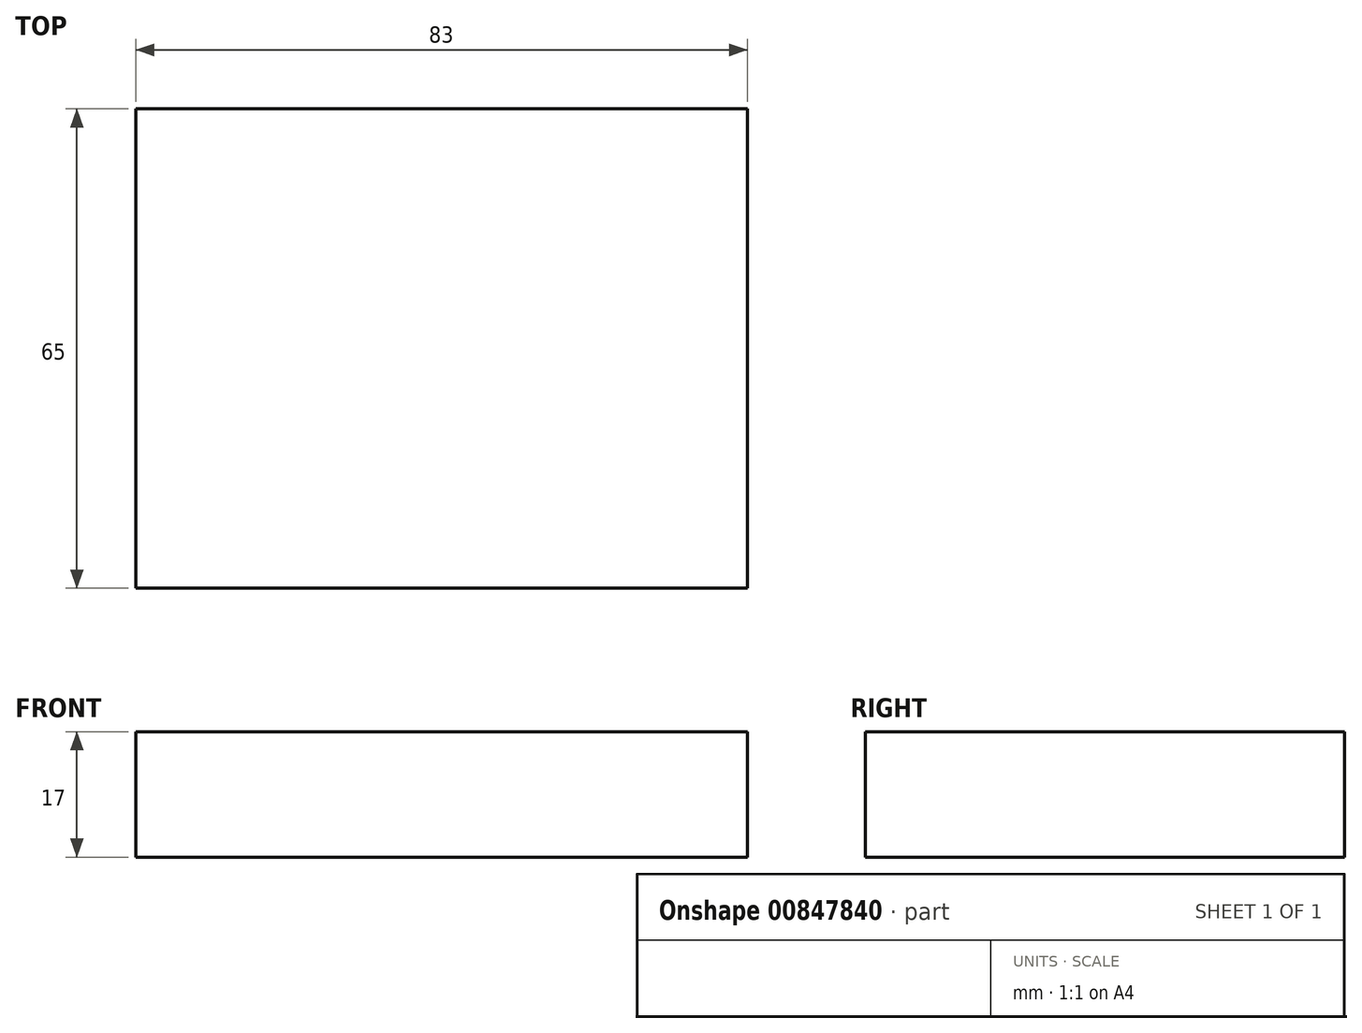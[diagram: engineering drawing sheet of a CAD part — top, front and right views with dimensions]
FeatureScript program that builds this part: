
annotation { "Feature Type Name" : "Feature", "Feature Type Description" : "" }
export const myFeature = defineFeature(function(context is Context, id is Id, definition is map)
    precondition{}
    {
        {
            var Q0;
            Q0=qCreatedBy(makeId("Front.planeOp"),FACE);
            var sketch = newSketch(context, id + "F0", { "sketchPlane" : qUnion([Q0])});
            skLineSegment(sketch, "E0.bottom", {"start": v(-41.5, 22) * mm, "end": v(41.5, 22) * mm});
            skLineSegment(sketch, "E0.top", {"start": v(-41.5, 5) * mm, "end": v(41.5, 5) * mm});
            skLineSegment(sketch, "E0.left", {"start": v(-41.5, 22) * mm, "end": v(-41.5, 5) * mm});
            skLineSegment(sketch, "E0.right", {"start": v(41.5, 22) * mm, "end": v(41.5, 5) * mm});
            skLineSegment(sketch, "E1", {"start": v(0, 43.59) * mm, "end": v(0, -15.2) * mm, "construction": true});
            skSolve(sketch);
        }
        {
            var Q0;
            Q0=makeQuery(id+"F0.imprint","IMPRINT",FACE,{"disambiguationData":[TD([[makeQuery(id+"F0.imprint","IMPRINT",EDGE,{"derivedFrom":sQuery(id+"F0.wireOp",EDGE,"E0.bottom")}),-1.0]])]});
            var Q1;
            Q1=sQuery(id+"F0.wireOp",EDGE,"E0.bottom");
            var Q2;
            Q2=sQuery(id+"F0.wireOp",EDGE,"E0.right");
            var Q3;
            Q3=sQuery(id+"F0.wireOp",EDGE,"E0.top");
            var Q4;
            Q4=sQuery(id+"F0.wireOp",EDGE,"E0.left");
            extrude(context, id + "F1", {"entities" : qUnion([Q0]), "surfaceEntities" : qUnion([Q1, Q2, Q3, Q4]), "endBound" : BoundingType.SYMMETRIC, "depth" : 65 * mm, "offsetDistance" : 25.4 * mm});
        }
    });
